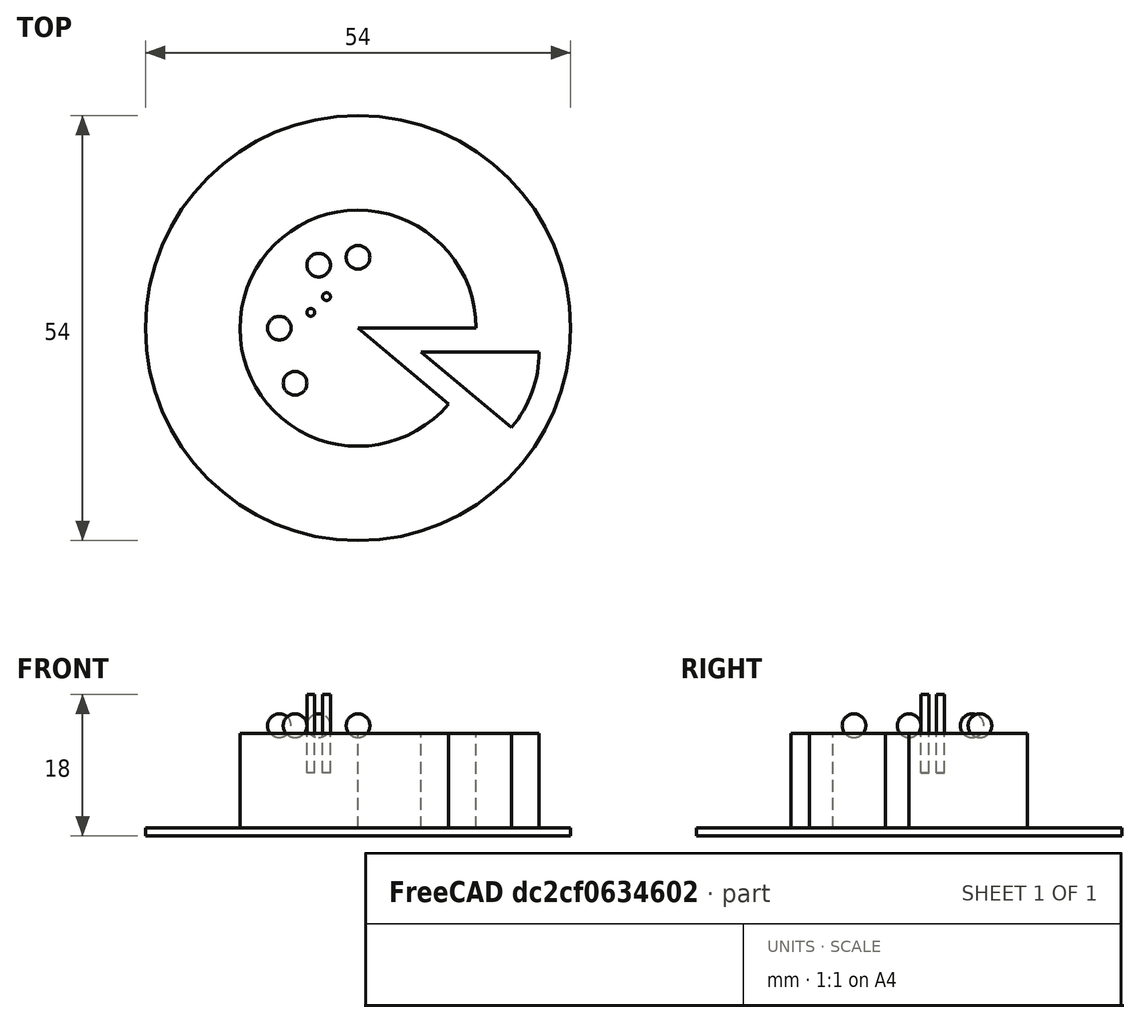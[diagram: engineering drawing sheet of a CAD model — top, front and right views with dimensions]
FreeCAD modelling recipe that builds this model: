
FCSTD DOCUMENT  (FreeCAD 0.19R24267 +99 (Git))
Label: Tarta
License: All rights reserved
LicenseURL: http://en.wikipedia.org/wiki/All_rights_reserved
objects: Part::Cylinder×5, Part::Sphere×4
note: 9 computed .brp shape members not serialized (recipe doc carries the construction recipe); baked Part::Feature solids carry a one-line shape summary decoded from their .brp

FEATURE [Part::Cylinder] Cylinder  label="Tarta"
  Angle = 320
  AttacherType = Attacher::AttachEngine3D
  Height = 12
  Placement = pos=(0,0,1) rot=(0,0,1;0rad)
  Radius = 15
FEATURE [Part::Cylinder] Cylinder001  label="Porcion"
  Angle = 40
  AttacherType = Attacher::AttachEngine3D
  Height = 12
  Placement = pos=(8,-3,1) rot=(0,0,1;5.58505rad)
  Radius = 15
FEATURE [Part::Cylinder] Cylinder002  label="Plato"
  Angle = 360
  AttacherType = Attacher::AttachEngine3D
  Height = 1
  Radius = 27
FEATURE [Part::Sphere] Sphere  label="Guinda1"
  Angle1 = -90
  Angle2 = 90
  Angle3 = 360
  AttacherType = Attacher::AttachEngine3D
  Placement = pos=(-10,0,14) rot=(0,0,1;0rad)
  Radius = 1.5
FEATURE [Part::Sphere] Sphere001  label="Guinda 2"
  Angle1 = -90
  Angle2 = 90
  Angle3 = 360
  AttacherType = Attacher::AttachEngine3D
  Placement = pos=(0,9,14) rot=(0,0,1;0rad)
  Radius = 1.5
FEATURE [Part::Sphere] Sphere002  label="Guinda 3"
  Angle1 = -90
  Angle2 = 90
  Angle3 = 360
  AttacherType = Attacher::AttachEngine3D
  Placement = pos=(-5,8,14) rot=(0,0,1;0rad)
  Radius = 1.5
FEATURE [Part::Sphere] Sphere003  label="Guinda 4"
  Angle1 = -90
  Angle2 = 90
  Angle3 = 360
  AttacherType = Attacher::AttachEngine3D
  Placement = pos=(-8,-7,14) rot=(0,0,1;0rad)
  Radius = 1.5
FEATURE [Part::Cylinder] Cylinder003  label="Vela 1"
  Angle = 360
  AttacherType = Attacher::AttachEngine3D
  Height = 10
  Placement = pos=(-4,4,8) rot=(0,0,1;0rad)
  Radius = 0.5
FEATURE [Part::Cylinder] Cylinder004  label="Vela 2"
  Angle = 360
  AttacherType = Attacher::AttachEngine3D
  Height = 10
  Placement = pos=(-6,2,8) rot=(0,0,1;0rad)
  Radius = 0.5
